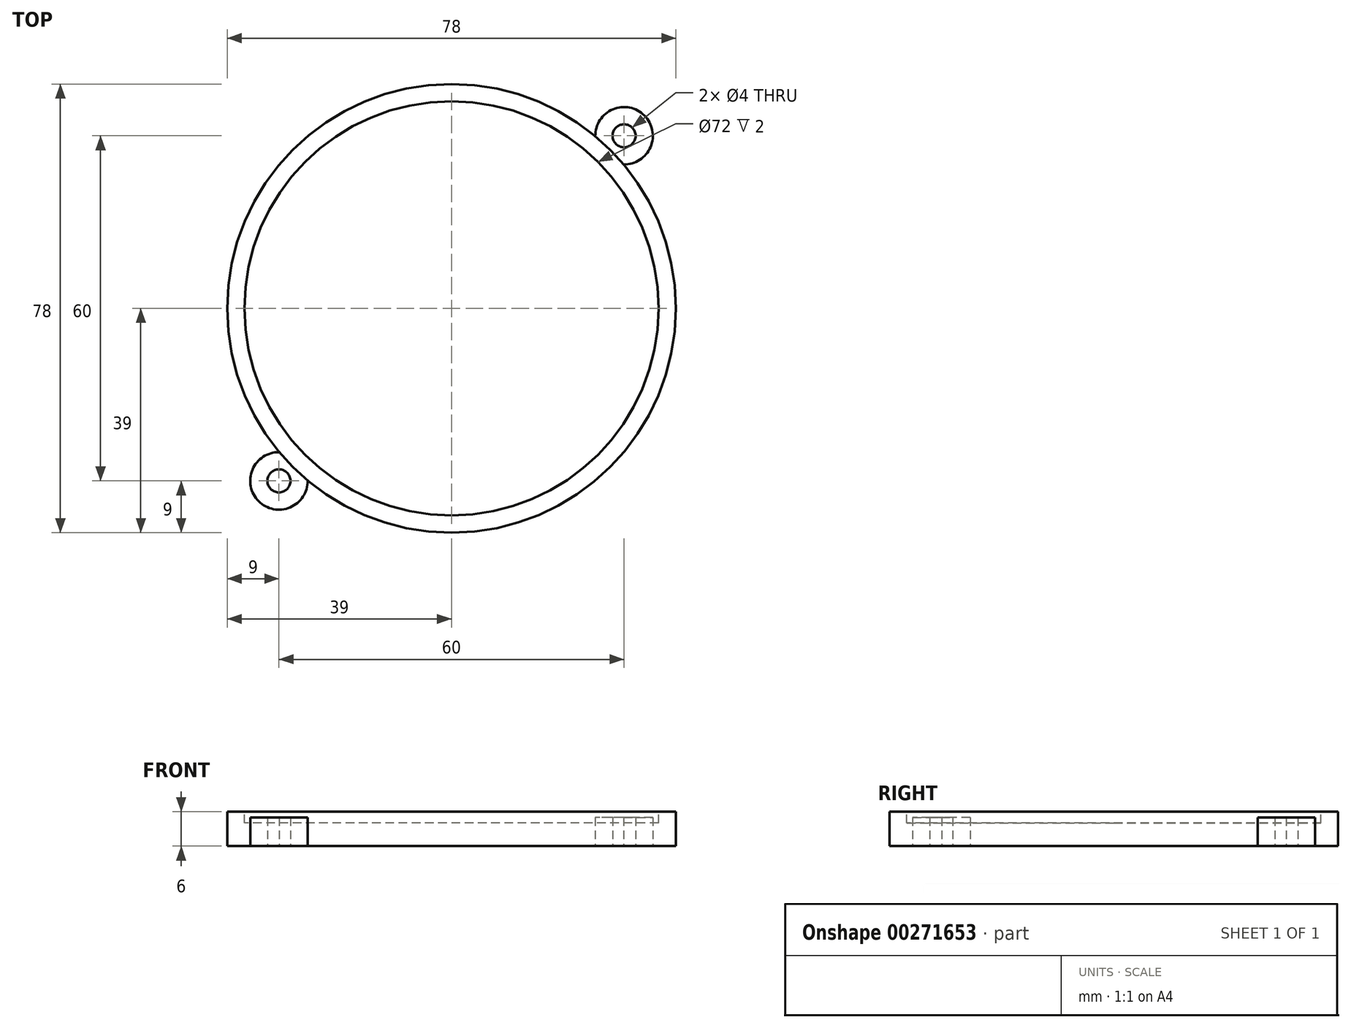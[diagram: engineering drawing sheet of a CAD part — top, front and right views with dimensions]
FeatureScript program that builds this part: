
annotation { "Feature Type Name" : "Feature", "Feature Type Description" : "" }
export const myFeature = defineFeature(function(context is Context, id is Id, definition is map)
    precondition{}
    {
        {
            var Q0;
            Q0=qCreatedBy(makeId("Front.planeOp"),FACE);
            var sketch = newSketch(context, id + "F0", { "sketchPlane" : qUnion([Q0])});
            skLineSegment(sketch, "E0.bottom", {"start": v(-39, 0) * mm, "end": v(0, 0) * mm});
            skLineSegment(sketch, "E1", {"start": v(0, 4) * mm, "end": v(0, 0) * mm});
            skLineSegment(sketch, "E2.0", {"start": v(-36, 4) * mm, "end": v(0, 4) * mm});
            skLineSegment(sketch, "E3", {"start": v(-36, 6) * mm, "end": v(-36, 4) * mm});
            skLineSegment(sketch, "E4.top", {"start": v(-39, 6) * mm, "end": v(-36, 6) * mm});
            skLineSegment(sketch, "E4.right", {"start": v(-36, 4) * mm, "end": v(-36, 6) * mm});
            skLineSegment(sketch, "E5", {"start": v(-39, 6) * mm, "end": v(-39, 0) * mm});
            skSolve(sketch);
        }
        {
            var Q0;
            Q0=qCreatedBy(makeId("Top.planeOp"),FACE);
            var sketch = newSketch(context, id + "F1", { "sketchPlane" : qUnion([Q0])});
            skCircle(sketch, "E6", {"center": v(30, 30) * mm, "radius": 5 * mm});
            skCircle(sketch, "E7.MirrorC", {"center": v(-30, 30) * mm, "radius": 5 * mm});
            skCircle(sketch, "E8.MirrorC", {"center": v(30, -30) * mm, "radius": 5 * mm});
            skCircle(sketch, "E9.MirrorC", {"center": v(-30, -30) * mm, "radius": 5 * mm});
            skCircle(sketch, "E10", {"center": v(30, 30) * mm, "radius": 2 * mm});
            skCircle(sketch, "E11.MirrorC", {"center": v(30, -30) * mm, "radius": 2 * mm});
            skCircle(sketch, "E12.MirrorC", {"center": v(-30, 30) * mm, "radius": 2 * mm});
            skCircle(sketch, "E13.MirrorC", {"center": v(-30, -30) * mm, "radius": 2 * mm});
            skSolve(sketch);
        }
        {
            var Q0;
            Q0=makeQuery(id+"F0.imprint","IMPRINT",FACE,{"disambiguationData":[TD([[makeQuery(id+"F0.imprint","IMPRINT",EDGE,{"derivedFrom":sQuery(id+"F0.wireOp",EDGE,"E0.bottom")}),1.0]])]});
            var Q1;
            Q1=sQuery(id+"F0.wireOp",EDGE,"E1");
            revolve(context, id + "F2", {"entities" : qUnion([Q0]), "axis" : qUnion([Q1]), "revolveType" : RevolveType.FULL});
        }
        {
            var Q0;
            Q0=makeQuery(id+"F1.imprint","IMPRINT",FACE,{"disambiguationData":[TD([[makeQuery(id+"F1.imprint","IMPRINT",EDGE,{"derivedFrom":sQuery(id+"F1.wireOp",EDGE,"E6")}),1.0]])]});
            var Q1;
            Q1=makeQuery(id+"F1.imprint","IMPRINT",FACE,{"disambiguationData":[TD([[makeQuery(id+"F1.imprint","IMPRINT",EDGE,{"derivedFrom":sQuery(id+"F1.wireOp",EDGE,"E7.MirrorC")}),-1.0]])]});
            var Q2;
            Q2=makeQuery(id+"F1.imprint","IMPRINT",FACE,{"disambiguationData":[TD([[makeQuery(id+"F1.imprint","IMPRINT",EDGE,{"derivedFrom":sQuery(id+"F1.wireOp",EDGE,"E9.MirrorC")}),1.0]])]});
            var Q3;
            Q3=makeQuery(id+"F1.imprint","IMPRINT",FACE,{"disambiguationData":[TD([[makeQuery(id+"F1.imprint","IMPRINT",EDGE,{"derivedFrom":sQuery(id+"F1.wireOp",EDGE,"E8.MirrorC")}),-1.0]])]});
            extrude(context, id + "F3", {"entities" : qUnion([Q0, Q1, Q2, Q3]), "operationType" : NewBodyOperationType.ADD, "depth" : 5 * mm});
        }
    });
